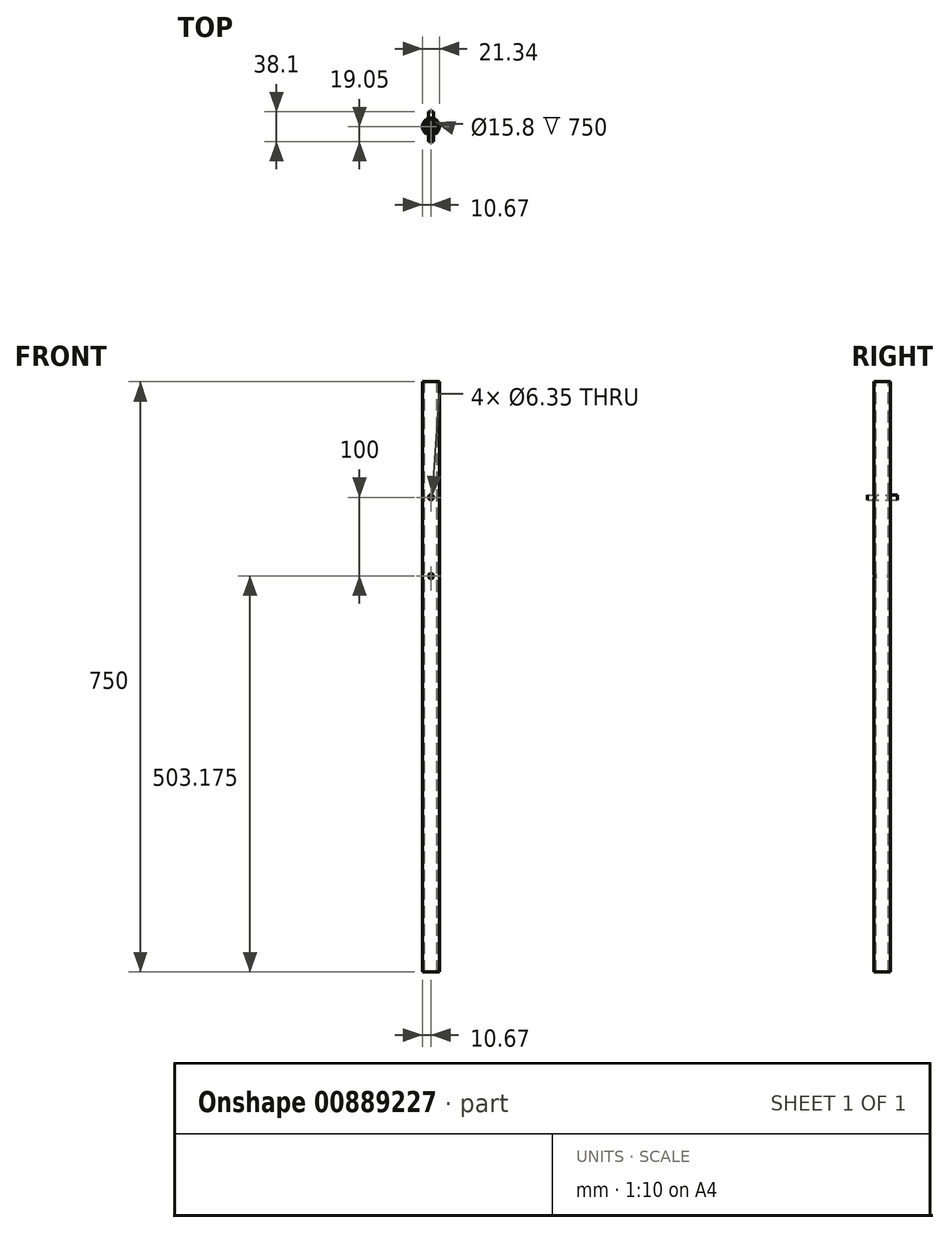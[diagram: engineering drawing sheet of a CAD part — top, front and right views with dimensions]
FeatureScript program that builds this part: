
annotation { "Feature Type Name" : "Feature", "Feature Type Description" : "" }
export const myFeature = defineFeature(function(context is Context, id is Id, definition is map)
    precondition{}
    {
        {
            var Q0;
            Q0=qCreatedBy(makeId("Top.planeOp"),FACE);
            var sketch = newSketch(context, id + "F0", { "sketchPlane" : qUnion([Q0])});
            skCircle(sketch, "E0", {"center": v(0, 0) * mm, "radius": 7.9 * mm});
            skCircle(sketch, "E1", {"center": v(0, 0) * mm, "radius": 10.67 * mm});
            skCircle(sketch, "E2", {"center": v(0, 0) * mm, "radius": 101.1 * mm});
            skCircle(sketch, "E3", {"center": v(0, 0) * mm, "radius": 109.54 * mm});
            skSolve(sketch);
        }
        {
            var Q0;
            Q0=makeQuery(id+"F0.imprint","IMPRINT",FACE,{"disambiguationData":[TD([[makeQuery(id+"F0.imprint","IMPRINT",EDGE,{"derivedFrom":sQuery(id+"F0.wireOp",EDGE,"E0")}),-1.0]])]});
            extrude(context, id + "F1", {"entities" : qUnion([Q0]), "oppositeDirection" : true, "depth" : 250 * mm * 3, "offsetDistance" : 25.4 * mm});
        }
        {
            var Q0;
            Q0=qCreatedBy(makeId("Front.planeOp"),FACE);
            var sketch = newSketch(context, id + "F2", { "sketchPlane" : qUnion([Q0])});
            skCircle(sketch, "E4", {"center": v(0, -146.82) * mm, "radius": 3.18 * mm});
            skCircle(sketch, "E5", {"center": v(0, -246.82) * mm, "radius": 3.18 * mm});
            skLineSegment(sketch, "E6", {"start": v(-5.83, -250) * mm, "end": v(5.66, -250) * mm, "construction": true});
            skLineSegment(sketch, "E7", {"start": v(-7.12, -150) * mm, "end": v(6.39, -150) * mm, "construction": true});
            skSolve(sketch);
        }
        {
            var Q0;
            Q0=makeQuery(id+"F2.imprint","IMPRINT",FACE,{"disambiguationData":[TD([[makeQuery(id+"F2.imprint","IMPRINT",EDGE,{"derivedFrom":sQuery(id+"F2.wireOp",EDGE,"E4")}),1.0]])]});
            var Q1;
            Q1=makeQuery(id+"F2.imprint","IMPRINT",FACE,{"disambiguationData":[TD([[makeQuery(id+"F2.imprint","IMPRINT",EDGE,{"derivedFrom":sQuery(id+"F2.wireOp",EDGE,"E5")}),1.0]])]});
            extrude(context, id + "F3", {"entities" : qUnion([Q0, Q1]), "operationType" : NewBodyOperationType.REMOVE, "endBound" : BoundingType.SYMMETRIC, "oppositeDirection" : true, "depth" : 25.4 * mm, "offsetDistance" : 25.4 * mm});
        }
        {
            var Q0;
            Q0=makeQuery(id+"F2.imprint","IMPRINT",FACE,{"disambiguationData":[TD([[makeQuery(id+"F2.imprint","IMPRINT",EDGE,{"derivedFrom":sQuery(id+"F2.wireOp",EDGE,"E4")}),1.0]])]});
            extrude(context, id + "F4", {"entities" : qUnion([Q0]), "endBound" : BoundingType.SYMMETRIC, "depth" : 38.1 * mm, "offsetDistance" : 25.4 * mm});
        }
    });
